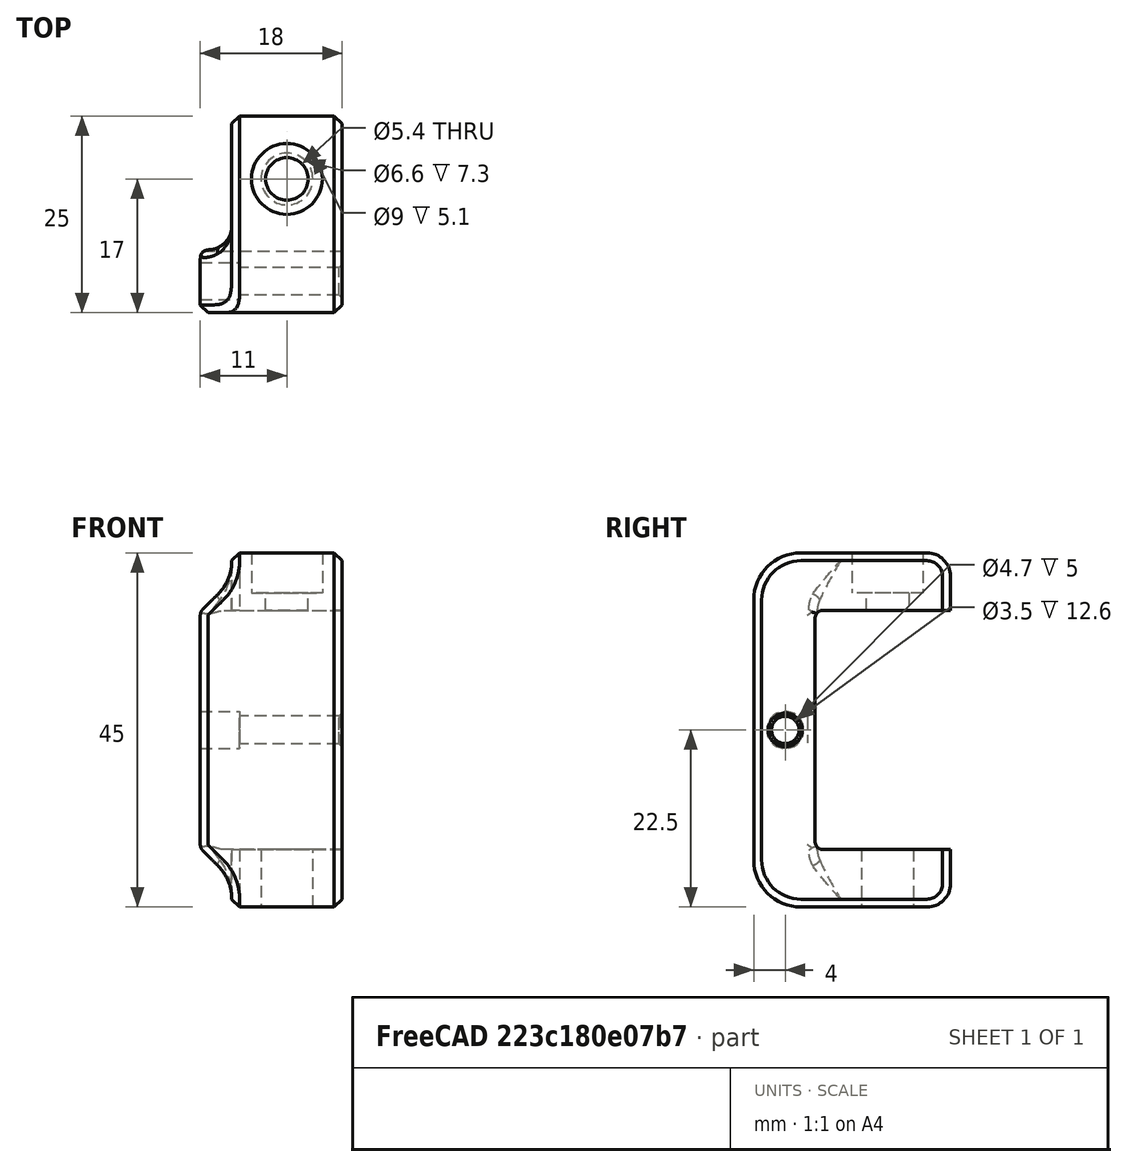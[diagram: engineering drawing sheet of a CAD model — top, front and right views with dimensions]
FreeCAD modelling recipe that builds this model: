
FCSTD DOCUMENT  (FreeCAD 0.18R16146 (Git))
Label: tesioner
License: Other
LicenseURL: GPL3
objects: Sketcher::SketchObject×2, Part::Feature×1, PartDesign::FeatureBase×1, PartDesign::Pad×1, PartDesign::Pocket×1, PartDesign::Body×1
note: 9 computed .brp shape members not serialized (recipe doc carries the construction recipe); baked Part::Feature solids carry a one-line shape summary decoded from their .brp

FEATURE [Part::Feature] Part__Feature294001  label="SOLID024"
  shape: bbox 18 x 25 x 45 mm, 83 faces (baked)
FEATURE [PartDesign::FeatureBase] BaseFeature
  BaseFeature = -> Part__Feature294001
FEATURE [Sketcher::SketchObject] Sketch
  MapMode = 5
  Placement = pos=(0,0,5.69224e-06) rot=(1,0,0;3.14159rad)
  Support = -> [BaseFeature]
  sketch-geometry (1):
    g0: Circle CenterX=0 CenterY=0 CenterZ=0 NormalX=0 NormalY=0 NormalZ=1 AngleXU=0 Radius=5
  constraints (1):
    c: Coincident(g0,g-1)
FEATURE [PartDesign::Pad] Pad
  BaseFeature = -> BaseFeature
  Length = 10
  Length2 = 100
  Profile = -> Sketch
  Type = 3
  UpToFace = -> BaseFeature [Face15]
FEATURE [Sketcher::SketchObject] Sketch001
  MapMode = 5
  Placement = pos=(0,0,5.69224e-06) rot=(1,0,0;3.14159rad)
  Support = -> [Pad]
  sketch-geometry (1):
    g0: Circle CenterX=0 CenterY=0 CenterZ=0 NormalX=0 NormalY=0 NormalZ=1 AngleXU=0 Radius=3.3
  constraints (2):
    c: Coincident(g0,g-1)
    c: Radius(g0) = 3.3
FEATURE [PartDesign::Pocket] Pocket
  BaseFeature = -> Pad
  Length = 0
  Length2 = 100
  Profile = -> Sketch001
  Type = 3
  UpToFace = -> Pad [Face73]
FEATURE [PartDesign::Body] Body
  BaseFeature = -> Part__Feature294001
  Group = -> [BaseFeature,Sketch,Pad,Sketch001,Pocket]
  Origin = -> Origin
  Tip = -> Pocket
